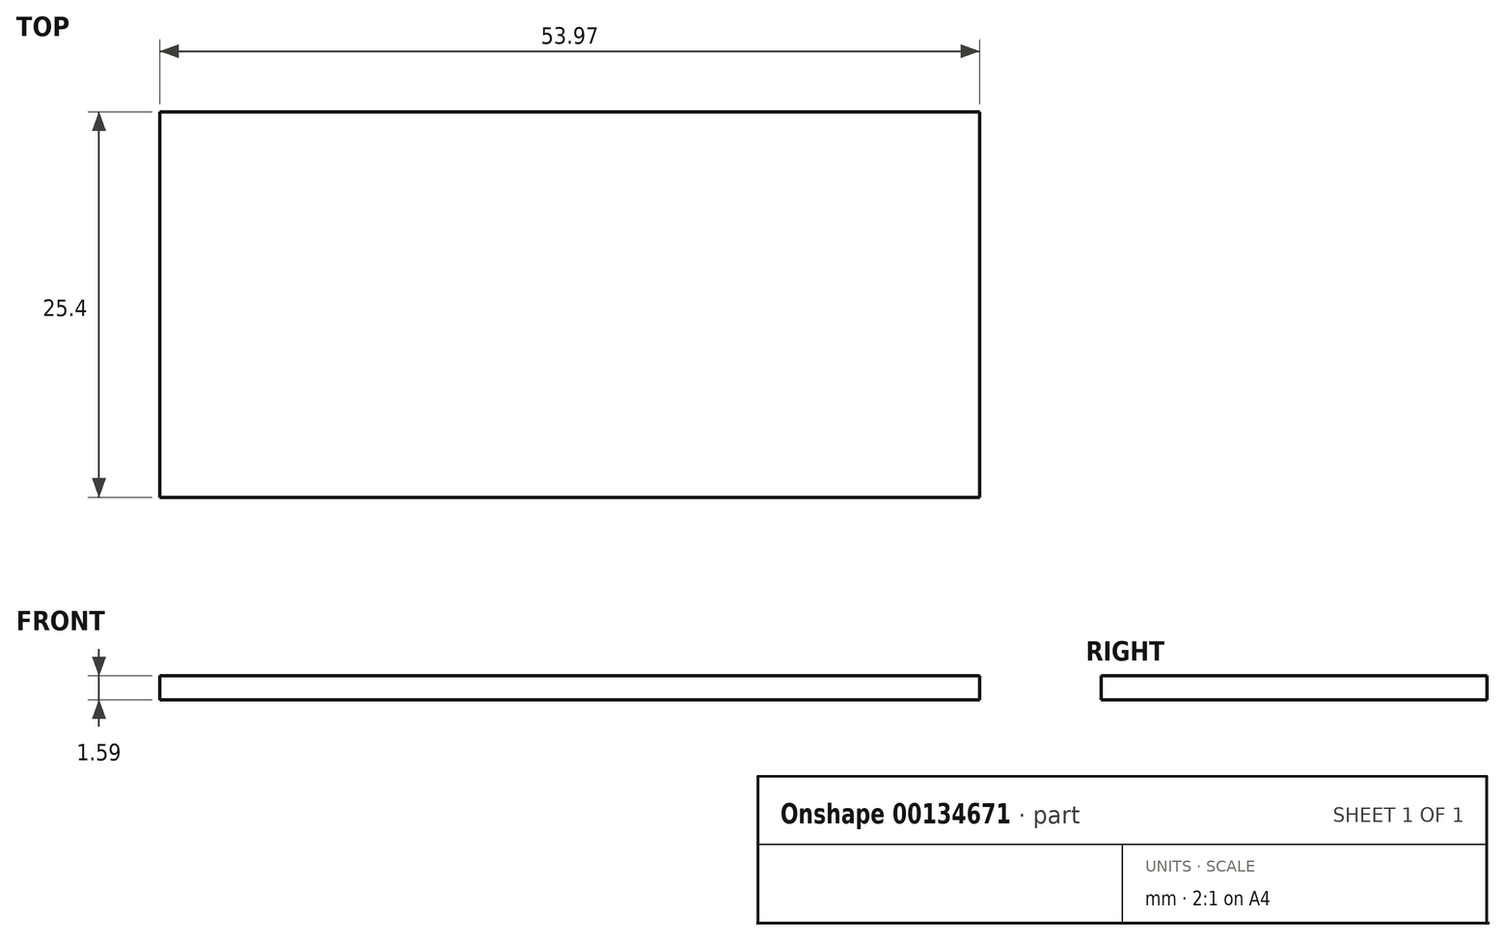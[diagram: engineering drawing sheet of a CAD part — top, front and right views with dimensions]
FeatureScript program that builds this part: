
annotation { "Feature Type Name" : "Feature", "Feature Type Description" : "" }
export const myFeature = defineFeature(function(context is Context, id is Id, definition is map)
    precondition{}
    {
        {
            var Q0;
            Q0=qCreatedBy(makeId("Top.planeOp"),FACE);
            var sketch = newSketch(context, id + "F0", { "sketchPlane" : qUnion([Q0])});
            skLineSegment(sketch, "E0.bottom", {"start": v(-70.47, 40.68) * mm, "end": v(-16.5, 40.68) * mm});
            skLineSegment(sketch, "E0.top", {"start": v(-70.47, 15.28) * mm, "end": v(-16.5, 15.28) * mm});
            skLineSegment(sketch, "E0.left", {"start": v(-70.47, 40.68) * mm, "end": v(-70.47, 15.28) * mm});
            skLineSegment(sketch, "E0.right", {"start": v(-16.5, 40.68) * mm, "end": v(-16.5, 15.28) * mm});
            skSolve(sketch);
        }
        {
            var Q0;
            Q0 = qSketchRegion(id + "F0", true);
            extrude(context, id + "F1", {"entities" : qUnion([Q0]), "depth" : 1.59 * mm});
        }
    });
